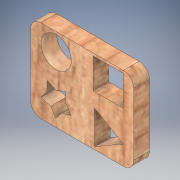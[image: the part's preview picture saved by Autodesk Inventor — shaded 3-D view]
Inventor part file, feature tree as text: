
AUTODESK INVENTOR PART (.ipt)
format: ipt  version: 2017 (Build 210142000, 142)  size: 224,768 bytes
history: native  units: in
note: dims shown in document units (in); Inventor stores cm internally (conversion verified against a paired STEP export)
features: extrude x2, shell x1, sketch x1, projected_geometry x1
ambient origin geometry x8: Origin, YZ Plane, XZ Plane, XY Plane, X Axis, Y Axis, Z Axis, Center Point
bodies: Solid1 (feature_tree)
feature tree (5):
  extrude  "Extrusion1"  Depth=1.59in
  extrude  "Extrusion2"  Depth=0.2in
  shell  "Shell1"  Thickness=0.3in
  sketch  "Sketch1"  dims[d0=1.975in d1=1.59in d2=0.2in d3=0.3in d4=0.0in d10=0.58in d11=0.05in d12=0.2in d13=0.58in d14=0.58in d15=0.58in d16=0.2in d17=0.05in d18=0.638in d19=0.2in d20=0.05in d21=0.605in d23=0.187in d25=0.187in d26=0.187in d27=0.187in d28=0.187in d29=0.187in d30=0.187in d31=0.187in d32=0.1869in d33=0.1541in d34=0.3in d35=0.0in d36=0.01in]
  projected_geometry  "Projected Loop1"
